# Revit family: NBS_DudleyIndustriesLimited_SntryTwlDspslBins_5.5LSanitaryWasteBin
name_source: partatom
category: Furniture
units: mm (PartAtom-declared; Revit-internal decimal feet)

## family parameters
Cut with Voids When Loaded = No
Host = Face
Render Appearance Source = Family Geometry
Room Calculation Point = No
Shared = No

## types (1)
- 5.5LSanitaryWasteBin
    AssetType = Fixed
    BIMObjectName = NBS_DudleyIndustriesLimited_SanitaryTowelDisposalBins_5.5LSanitaryWasteBin
    BinMaterial = NBS_DudleyIndustriesLimited_StainlessSteel_Brushed
    Category = Pr_40_50_07_76:Sanitary towel disposal bins
    Default Elevation = 800 mm  [stored 2.62467 ft]
    Description = Compact and sleek Stainless steel sanitary waste unit, incorporating a holder for waste bags with a convenient bin below.
    DurationUnit = year
    Finish = Powder-coated,Brushed
    FinishAndColour = Powder-coated, white,Powder-coated, black,Brushed stainless steel
    Form = Wall-mounted, swing flap
    Height = 460 mm  [stored 1.50919 ft]
    IfcExportAs = IfcFurnitureType
    IfcExportType = USERDEFINED
    IntegralAccessories = Integrated waste bag holder.Inner liner.Front panel lock
    ManufacturerName = Dudley Industries Limited
    ManufacturerURL = https://www.dudleyindustries.com
    Material = Stainless steel
    ModelReference = 5.5L Sanitary Waste Bin
    NBSInstanceId = c4d575da-6535-43e5-8f8f-1c51e34eb022
    NBSObjectId = 647ade6a-8243-47c2-a3d6-7d58d25c0f93
    NBSVariantId = 00000000-0000-0000-0000-000000000000
    Name = SanitaryTowelDisposalBins_5.5LSanitaryWasteBin_DudleyIndustriesLimited
    NominalHeight = 0 mm  [stored 0 ft]
    NominalLength = 0 mm  [stored 0 ft]
    NominalWidth = 0 mm  [stored 0 ft]
    ProductInformation = https://source.thenbs.com
    Shape = Rectangle
    Size = 5.5 L
    Uniclass2015Code = Pr_40_50_07_76
    Uniclass2015Title = Sanitary towel disposal bins
    Uniclass2015Version = Products v1.36
    Version = 1
    WarrantyDescription = Ten year
    WarrantyDurationUnit = year

note: [stored X ft] marks values corroborated as IEEE doubles in the binary element streams (Revit-internal decimal feet)

## geometry (parser evidence)
native form markers: Sweep x3
no freeform markers — native parametric forms only
